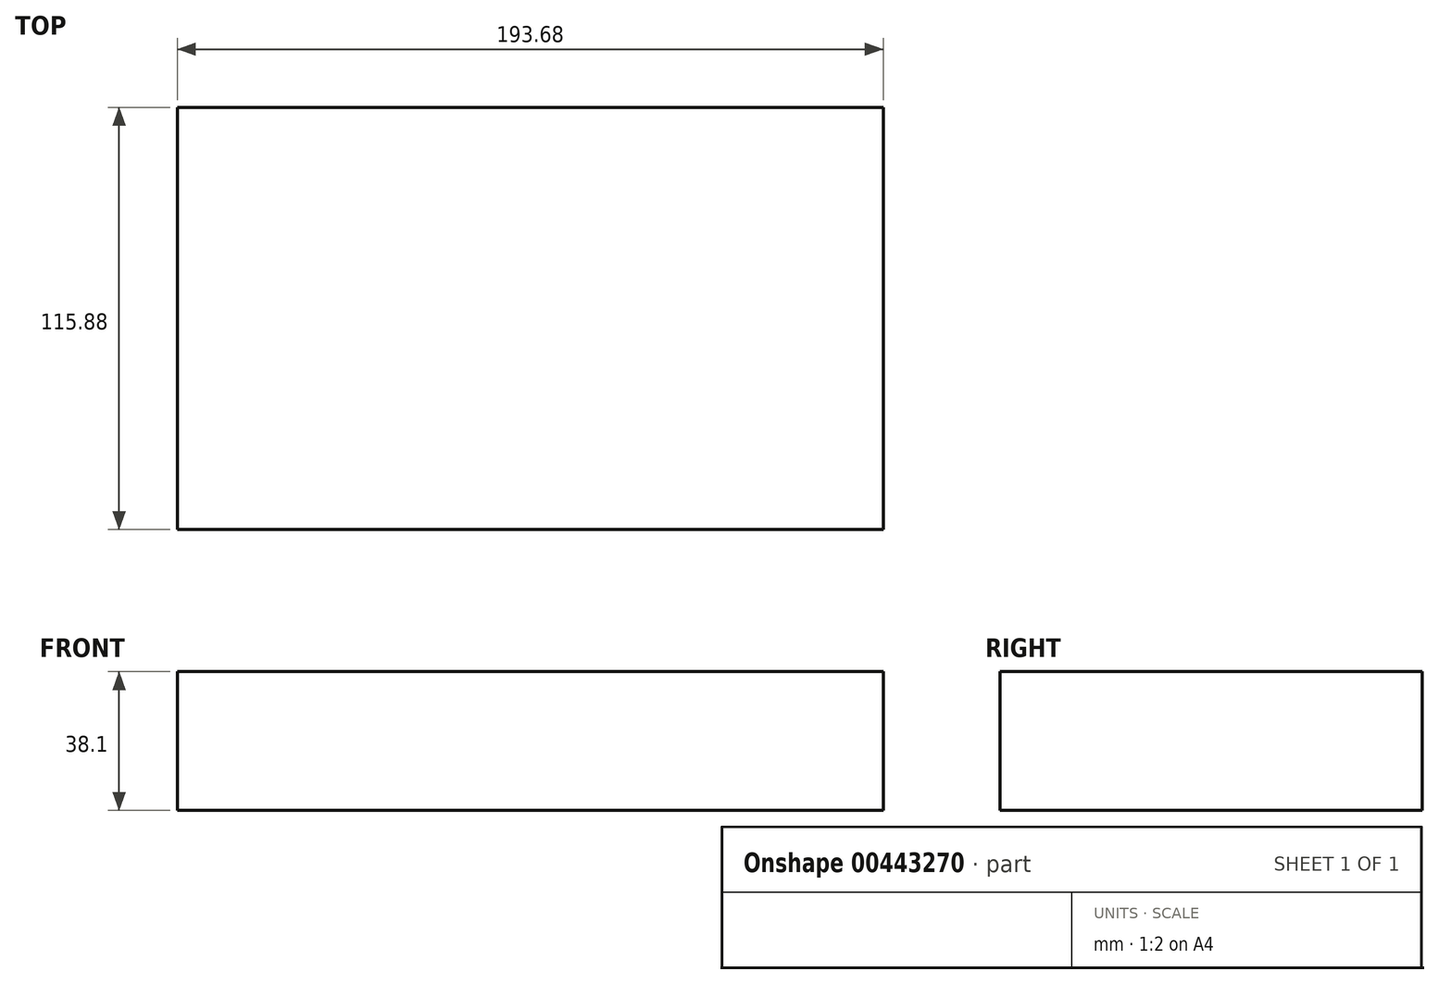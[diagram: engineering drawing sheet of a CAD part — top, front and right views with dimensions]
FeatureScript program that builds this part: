
annotation { "Feature Type Name" : "Feature", "Feature Type Description" : "" }
export const myFeature = defineFeature(function(context is Context, id is Id, definition is map)
    precondition{}
    {
        {
            var Q0;
            Q0=qCreatedBy(makeId("Top.planeOp"),FACE);
            var sketch = newSketch(context, id + "F0", { "sketchPlane" : qUnion([Q0])});
            skLineSegment(sketch, "E0.bottom", {"start": v(96.84, -57.94) * mm, "end": v(-96.84, -57.94) * mm});
            skLineSegment(sketch, "E0.top", {"start": v(96.84, 57.94) * mm, "end": v(-96.84, 57.94) * mm});
            skLineSegment(sketch, "E0.left", {"start": v(96.84, -57.94) * mm, "end": v(96.84, 57.94) * mm});
            skLineSegment(sketch, "E0.right", {"start": v(-96.84, -57.94) * mm, "end": v(-96.84, 57.94) * mm});
            skPoint(sketch, "E0.middle", {"position": v(0, 0) * mm});
            skSolve(sketch);
        }
        {
            var Q0;
            Q0=makeQuery(id+"F0.imprint","IMPRINT",FACE,{"disambiguationData":[TD([[makeQuery(id+"F0.imprint","IMPRINT",EDGE,{"derivedFrom":sQuery(id+"F0.wireOp",EDGE,"E0.bottom")}),-1.0]])]});
            extrude(context, id + "F1", {"entities" : qUnion([Q0]), "depth" : 38.1 * mm});
        }
    });
